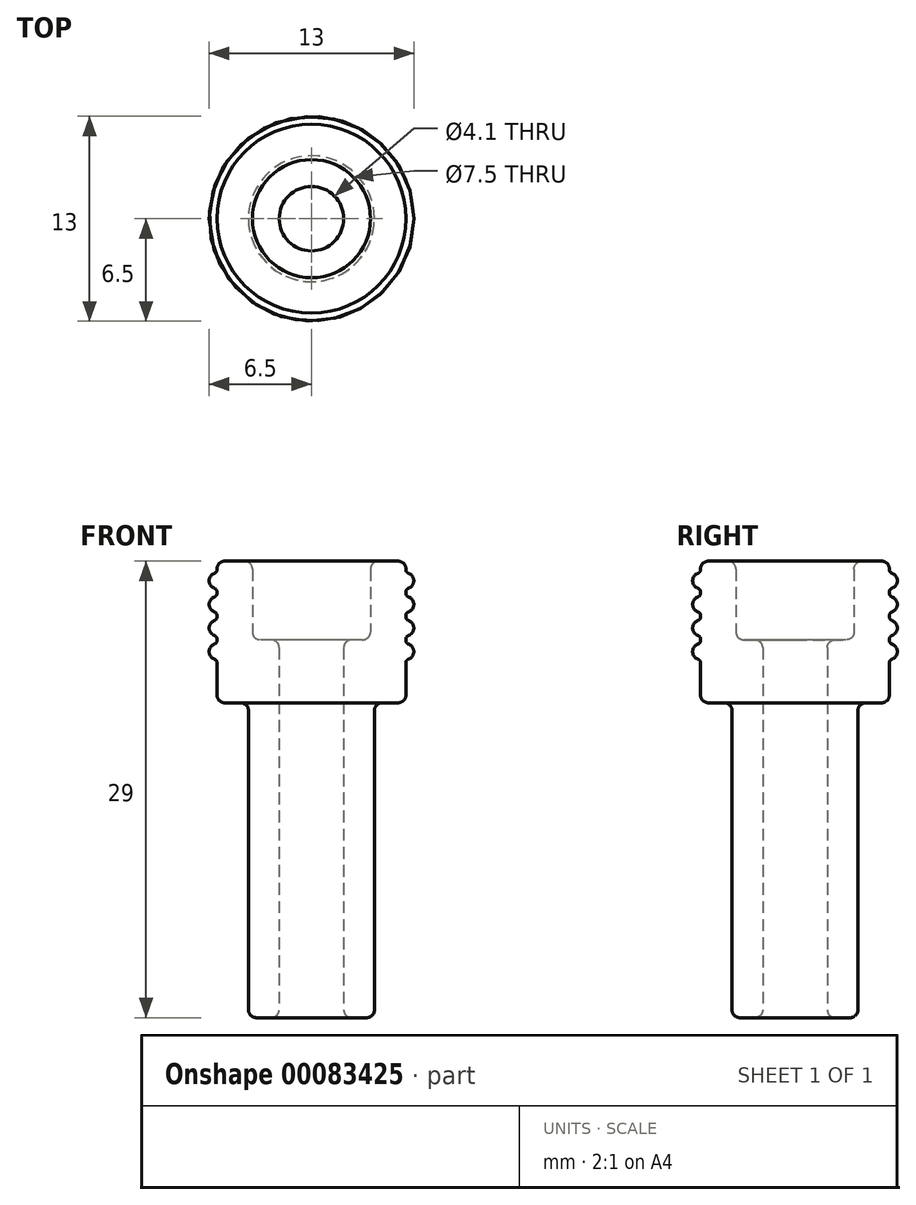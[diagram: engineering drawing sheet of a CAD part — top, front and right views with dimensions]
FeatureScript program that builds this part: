
annotation { "Feature Type Name" : "Feature", "Feature Type Description" : "" }
export const myFeature = defineFeature(function(context is Context, id is Id, definition is map)
    precondition{}
    {
        {
            var Q0;
            Q0=qCreatedBy(makeId("Top.planeOp"),FACE);
            var sketch = newSketch(context, id + "F0", { "sketchPlane" : qUnion([Q0])});
            skCircle(sketch, "E0", {"center": v(0, 0) * mm, "radius": 2.05 * mm});
            skCircle(sketch, "E1", {"center": v(0, 0) * mm, "radius": 6 * mm});
            skSolve(sketch);
        }
        {
            var Q0;
            Q0 = qSketchRegion(id + "F0", true);
            extrude(context, id + "F1", {"entities" : qUnion([Q0]), "depth" : 4 * mm});
        }
        {
            var Q0;
            Q0=makeQuery(id+"F1.opExtrude","CAP_FACE",FACE,{"disambiguationData":[OSD([sQuery(id+"F0.wireOp",EDGE,"E0"),sQuery(id+"F0.wireOp",EDGE,"E1")])],"isStart":false});
            var sketch = newSketch(context, id + "F2", { "sketchPlane" : qUnion([Q0])});
            skCircle(sketch, "E2", {"center": v(0, 0) * mm, "radius": 3.75 * mm});
            skCircle(sketch, "E3.0", {"center": v(0, 0) * mm, "radius": 6 * mm});
            skSolve(sketch);
        }
        {
            var Q0;
            Q0 = qSketchRegion(id + "F2", true);
            extrude(context, id + "F3", {"entities" : qUnion([Q0]), "operationType" : NewBodyOperationType.ADD, "depth" : 5 * mm});
        }
        {
            var Q0;
            Q0=makeQuery(id+"F1.opExtrude","CAP_FACE",FACE,{"disambiguationData":[OSD([sQuery(id+"F0.wireOp",EDGE,"E0"),sQuery(id+"F0.wireOp",EDGE,"E1")])],"isStart":false});
            var Q1;
            Q1=makeQuery(id+"F3.opExtrude","CAP_FACE",FACE,{"disambiguationData":[OSD([sQuery(id+"F2.wireOp",EDGE,"E2"),sQuery(id+"F2.wireOp",EDGE,"E3.0")])],"isStart":false});
            fillet(context, id + "F4", {"entities" : qUnion([Q0, Q1]), "radius" : .5 * mm, "tangentPropagation" : true, "allowEdgeOverflow" : false});
        }
        {
            var Q0;
            Q0=makeQuery(id+"F1.opExtrude","CAP_FACE",FACE,{"disambiguationData":[OSD([sQuery(id+"F0.wireOp",EDGE,"E0"),sQuery(id+"F0.wireOp",EDGE,"E1")])],"isStart":true});
            var sketch = newSketch(context, id + "F5", { "sketchPlane" : qUnion([Q0])});
            skCircle(sketch, "E4.0", {"center": v(0, 0) * mm, "radius": 2.05 * mm});
            skCircle(sketch, "E5", {"center": v(0, 0) * mm, "radius": 4 * mm});
            skSolve(sketch);
        }
        {
            var Q0;
            Q0 = qSketchRegion(id + "F5", true);
            extrude(context, id + "F6", {"entities" : qUnion([Q0]), "operationType" : NewBodyOperationType.ADD, "depth" : 20 * mm});
        }
        {
            var Q0;
            Q0=makeQuery(id+"F1.opExtrude","CAP_FACE",FACE,{"disambiguationData":[OSD([sQuery(id+"F0.wireOp",EDGE,"E0"),sQuery(id+"F0.wireOp",EDGE,"E1")])],"isStart":true});
            var Q1;
            Q1=makeQuery(id+"F6.opExtrude","CAP_FACE",FACE,{"disambiguationData":[OSD([sQuery(id+"F5.wireOp",EDGE,"E4.0"),sQuery(id+"F5.wireOp",EDGE,"E5")])],"isStart":false});
            fillet(context, id + "F7", {"entities" : qUnion([Q0, Q1]), "radius" : .5 * mm, "tangentPropagation" : true, "allowEdgeOverflow" : false});
        }
        {
            var Q0;
            Q0=qCreatedBy(makeId("Front.planeOp"),FACE);
            var sketch = newSketch(context, id + "F8", { "sketchPlane" : qUnion([Q0])});
            skLineSegment(sketch, "E6", {"start": v(-6, 0.5) * mm, "end": v(-6, 8.5) * mm});
            skLineSegment(sketch, "E7", {"start": v(6, 8.5) * mm, "end": v(6, 0.5) * mm});
            skCircle(sketch, "E8", {"center": v(-6, 7.75) * mm, "radius": 0.5 * mm});
            skCircle(sketch, "E9", {"center": v(-6, 6.25) * mm, "radius": 0.5 * mm});
            skCircle(sketch, "E10", {"center": v(-6, 4.75) * mm, "radius": 0.5 * mm});
            skCircle(sketch, "E11", {"center": v(-6, 3.25) * mm, "radius": 0.5 * mm});
            skSolve(sketch);
        }
        {
            var Q0;
            Q0 = qSketchRegion(id + "F8", true);
            var Q1;
            Q1=makeQuery(id+"F3.boolean.opBoolean","MERGE",FACE,{"derivedFrom":[makeQuery(id+"F1.opExtrude","SWEPT_FACE",FACE,{"disambiguationData":[OSD([sQuery(id+"F0.wireOp",EDGE,"E1")])]}),makeQuery(id+"F3.opExtrude","SWEPT_FACE",FACE,{"disambiguationData":[OSD([sQuery(id+"F2.wireOp",EDGE,"E3.0")])]})]});
            revolve(context, id + "F9", {"operationType" : NewBodyOperationType.ADD, "entities" : qUnion([Q0]), "axis" : qUnion([Q1]), "revolveType" : RevolveType.FULL});
        }
        {
            var Q0;
            Q0=makeQuery(id+"F9.boolean.opBoolean","SPLIT",FACE,{"disambiguationData":[TD([makeQuery(id+"F9.opRevolve","SWEPT_FACE",FACE,{"disambiguationData":[OSD([sQuery(id+"F8.wireOp",EDGE,"E8")])]}),makeQuery(id+"F9.opRevolve","SWEPT_FACE",FACE,{"disambiguationData":[OSD([sQuery(id+"F8.wireOp",EDGE,"E9")])]})])],"derivedFrom":makeQuery(id+"F3.boolean.opBoolean","MERGE",FACE,{"derivedFrom":[makeQuery(id+"F1.opExtrude","SWEPT_FACE",FACE,{"disambiguationData":[OSD([sQuery(id+"F0.wireOp",EDGE,"E1")])]}),makeQuery(id+"F3.opExtrude","SWEPT_FACE",FACE,{"disambiguationData":[OSD([sQuery(id+"F2.wireOp",EDGE,"E3.0")])]})]})});
            var Q1;
            Q1=makeQuery(id+"F9.boolean.opBoolean","SPLIT",FACE,{"disambiguationData":[TD([makeQuery(id+"F9.opRevolve","SWEPT_FACE",FACE,{"disambiguationData":[OSD([sQuery(id+"F8.wireOp",EDGE,"E9")])]}),makeQuery(id+"F9.opRevolve","SWEPT_FACE",FACE,{"disambiguationData":[OSD([sQuery(id+"F8.wireOp",EDGE,"E10")])]})])],"derivedFrom":makeQuery(id+"F3.boolean.opBoolean","MERGE",FACE,{"derivedFrom":[makeQuery(id+"F1.opExtrude","SWEPT_FACE",FACE,{"disambiguationData":[OSD([sQuery(id+"F0.wireOp",EDGE,"E1")])]}),makeQuery(id+"F3.opExtrude","SWEPT_FACE",FACE,{"disambiguationData":[OSD([sQuery(id+"F2.wireOp",EDGE,"E3.0")])]})]})});
            var Q2;
            Q2=makeQuery(id+"F9.boolean.opBoolean","SPLIT",FACE,{"disambiguationData":[TD([makeQuery(id+"F9.opRevolve","SWEPT_FACE",FACE,{"disambiguationData":[OSD([sQuery(id+"F8.wireOp",EDGE,"E10")])]}),makeQuery(id+"F9.opRevolve","SWEPT_FACE",FACE,{"disambiguationData":[OSD([sQuery(id+"F8.wireOp",EDGE,"E11")])]})])],"derivedFrom":makeQuery(id+"F3.boolean.opBoolean","MERGE",FACE,{"derivedFrom":[makeQuery(id+"F1.opExtrude","SWEPT_FACE",FACE,{"disambiguationData":[OSD([sQuery(id+"F0.wireOp",EDGE,"E1")])]}),makeQuery(id+"F3.opExtrude","SWEPT_FACE",FACE,{"disambiguationData":[OSD([sQuery(id+"F2.wireOp",EDGE,"E3.0")])]})]})});
            var Q3;
            {var subQ0=sQuery(id+"F0.wireOp",EDGE,"E1");Q3=makeQuery(id+"F9.boolean.opBoolean","SPLIT",FACE,{"disambiguationData":[TD([makeQuery(id+"F7.opFillet","BLEND_FACE",FACE,{"disambiguationData":[OSD([subQ0])]}),makeQuery(id+"F9.opRevolve","SWEPT_FACE",FACE,{"disambiguationData":[OSD([sQuery(id+"F8.wireOp",EDGE,"E11")])]})])],"derivedFrom":makeQuery(id+"F3.boolean.opBoolean","MERGE",FACE,{"derivedFrom":[makeQuery(id+"F1.opExtrude","SWEPT_FACE",FACE,{"disambiguationData":[OSD([subQ0])]}),makeQuery(id+"F3.opExtrude","SWEPT_FACE",FACE,{"disambiguationData":[OSD([sQuery(id+"F2.wireOp",EDGE,"E3.0")])]})]})});}
            var Q4;
            {var subQ0=sQuery(id+"F2.wireOp",EDGE,"E3.0");Q4=makeQuery(id+"F9.boolean.opBoolean","SPLIT",FACE,{"disambiguationData":[TD([makeQuery(id+"F4.opFillet","BLEND_FACE",FACE,{"disambiguationData":[OSD([subQ0])]}),makeQuery(id+"F9.opRevolve","SWEPT_FACE",FACE,{"disambiguationData":[OSD([sQuery(id+"F8.wireOp",EDGE,"E8")])]})])],"derivedFrom":makeQuery(id+"F3.boolean.opBoolean","MERGE",FACE,{"derivedFrom":[makeQuery(id+"F1.opExtrude","SWEPT_FACE",FACE,{"disambiguationData":[OSD([sQuery(id+"F0.wireOp",EDGE,"E1")])]}),makeQuery(id+"F3.opExtrude","SWEPT_FACE",FACE,{"disambiguationData":[OSD([subQ0])]})]})});}
            fillet(context, id + "F10", {"entities" : qUnion([Q0, Q1, Q2, Q3, Q4]), "radius" : .25 * mm, "tangentPropagation" : true, "allowEdgeOverflow" : false});
        }
    });
